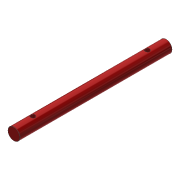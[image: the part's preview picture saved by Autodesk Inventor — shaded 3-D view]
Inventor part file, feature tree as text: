
AUTODESK INVENTOR PART (.ipt)
format: ipt  version: 2019.4 (Build 234330000, 330)  size: 94,720 bytes
history: native  units: mm
features: extrude x2, sketch x2, other x1, chamfer x1
ambient origin geometry x8: Origin, YZ Plane, XZ Plane, XY Plane, X Axis, Y Axis, Z Axis, Center Point
bodies: Body1 (feature_tree)
feature tree (6):
  other  "ソリッド1"
  extrude  "押し出し1"  Depth=4.0mm
  chamfer  "面取り1"  Distance=48.0mm
  extrude  "押し出し2"  Depth=2.0mm TaperAngle=45.0deg
  sketch  "スケッチ1"
  sketch  "スケッチ2"
